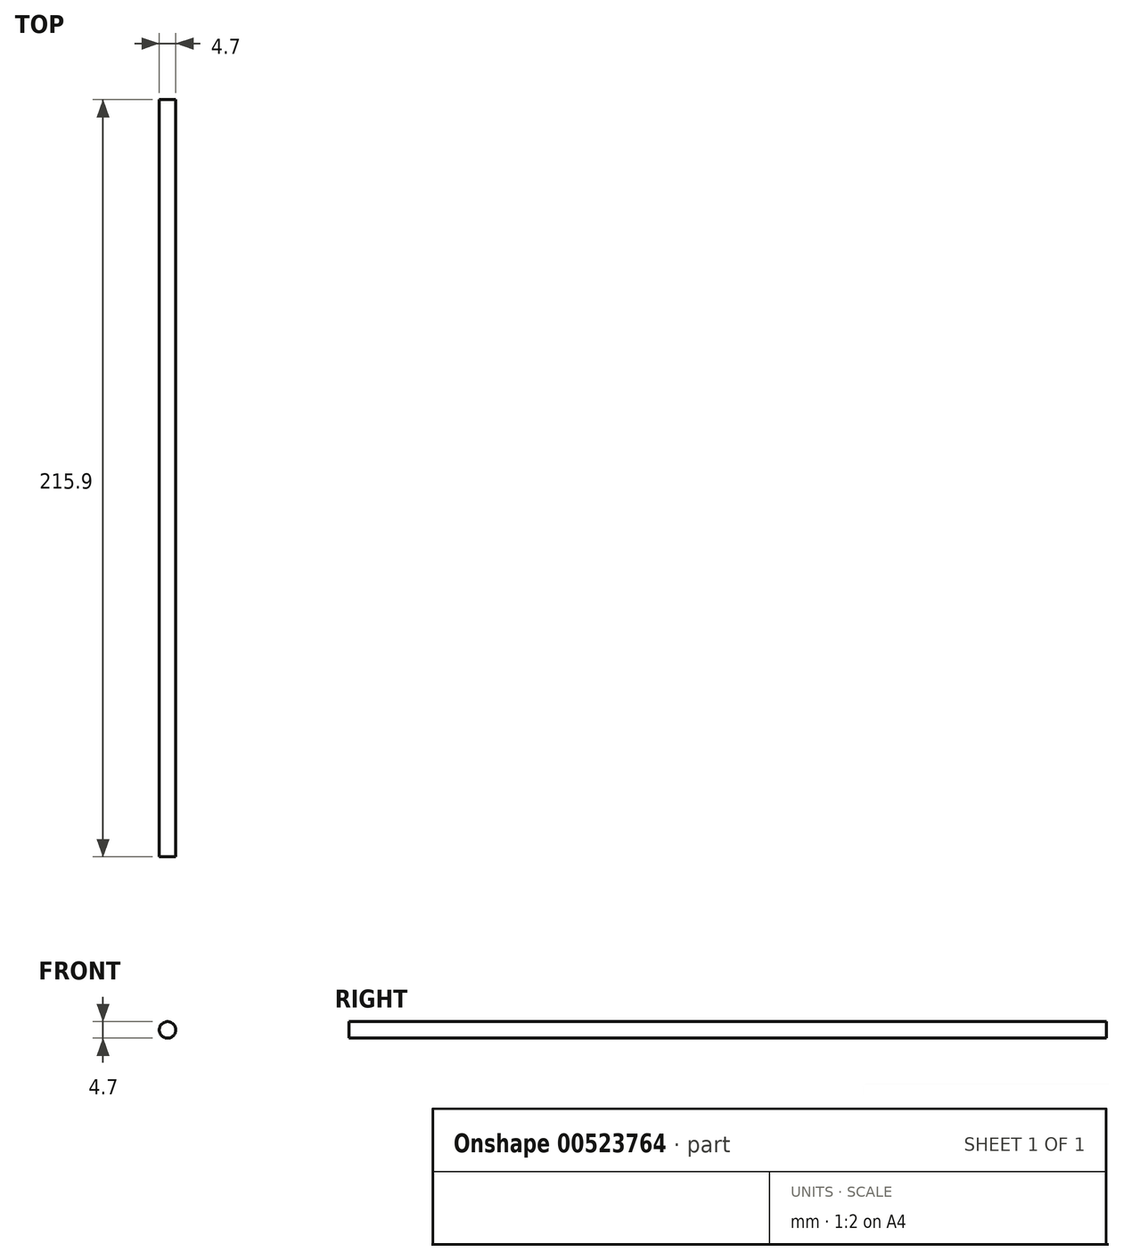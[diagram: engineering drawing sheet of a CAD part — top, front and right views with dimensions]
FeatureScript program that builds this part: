
annotation { "Feature Type Name" : "Feature", "Feature Type Description" : "" }
export const myFeature = defineFeature(function(context is Context, id is Id, definition is map)
    precondition{}
    {
        {
            var Q0;
            Q0=qCreatedBy(makeId("Front.planeOp"),FACE);
            var sketch = newSketch(context, id + "F0", { "sketchPlane" : qUnion([Q0])});
            skCircle(sketch, "E0", {"center": v(0, 0) * mm, "radius": 2.35 * mm});
            skSolve(sketch);
        }
        {
            var Q0;
            Q0=makeQuery(id+"F0.imprint","IMPRINT",FACE,{"disambiguationData":[TD([[makeQuery(id+"F0.imprint","IMPRINT",EDGE,{"derivedFrom":sQuery(id+"F0.wireOp",EDGE,"E0")}),1.0]])]});
            extrude(context, id + "F1", {"entities" : qUnion([Q0]), "depth" : 215.9 * mm, "offsetDistance" : 25.4 * mm});
        }
    });
